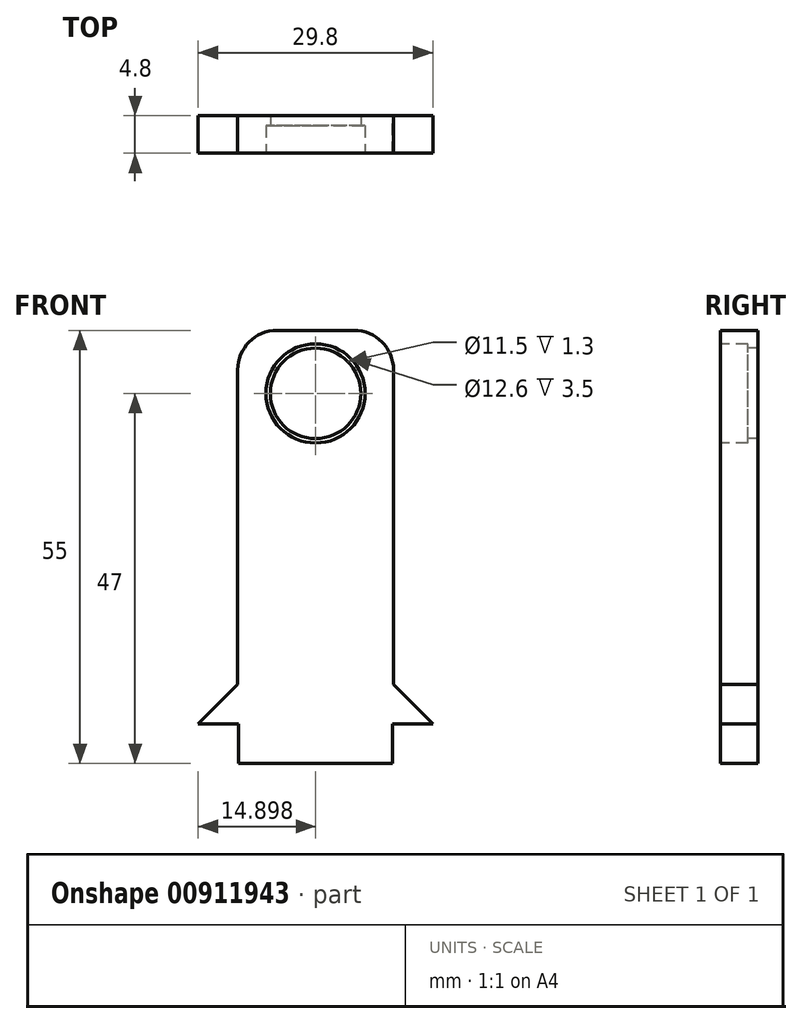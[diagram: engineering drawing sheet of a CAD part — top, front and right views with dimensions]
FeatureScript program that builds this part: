
annotation { "Feature Type Name" : "Feature", "Feature Type Description" : "" }
export const myFeature = defineFeature(function(context is Context, id is Id, definition is map)
    precondition{}
    {
        {
            var Q0;
            Q0=qCreatedBy(makeId("Front.planeOp"),FACE);
            var sketch = newSketch(context, id + "F0", { "sketchPlane" : qUnion([Q0])});
            skLineSegment(sketch, "E0.bottom", {"start": v(-10.83, 44.31) * mm, "end": v(8.97, 44.31) * mm});
            skLineSegment(sketch, "E0.top", {"start": v(-10.83, -10.69) * mm, "end": v(8.97, -10.69) * mm});
            skLineSegment(sketch, "E0.left", {"start": v(-10.83, 44.31) * mm, "end": v(-10.83, -10.69) * mm});
            skLineSegment(sketch, "E0.right", {"start": v(8.97, 44.31) * mm, "end": v(8.97, -10.69) * mm});
            skSolve(sketch);
        }
        {
            var Q0;
            Q0 = qSketchRegion(id + "F0", true);
            extrude(context, id + "F1", {"entities" : qUnion([Q0]), "depth" : 4.8 * mm, "offsetDistance" : 25 * mm});
        }
        {
            var Q0;
            Q0=makeQuery(id+"F1.opExtrude","CAP_FACE",FACE,{"disambiguationData":[OSD([sQuery(id+"F0.wireOp",EDGE,"E0.bottom"),sQuery(id+"F0.wireOp",EDGE,"E0.top"),sQuery(id+"F0.wireOp",EDGE,"E0.left"),sQuery(id+"F0.wireOp",EDGE,"E0.right")])],"isStart":false});
            var sketch = newSketch(context, id + "F2", { "sketchPlane" : qUnion([Q0])});
            skCircle(sketch, "E1", {"center": v(-0.93, 36.31) * mm, "radius": 5.75 * mm});
            skLineSegment(sketch, "E2", {"start": v(-0.93, -10.69) * mm, "end": v(-0.93, 44.31) * mm, "construction": true});
            skSolve(sketch);
        }
        {
            var Q0;
            Q0 = qSketchRegion(id + "F2", true);
            extrude(context, id + "F3", {"entities" : qUnion([Q0]), "operationType" : NewBodyOperationType.REMOVE, "endBound" : BoundingType.UP_TO_NEXT, "oppositeDirection" : true, "depth" : 25 * mm, "offsetDistance" : 25 * mm});
        }
        {
            var Q0;
            Q0=makeQuery(id+"F1.opExtrude","CAP_FACE",FACE,{"disambiguationData":[OSD([sQuery(id+"F0.wireOp",EDGE,"E0.bottom"),sQuery(id+"F0.wireOp",EDGE,"E0.top"),sQuery(id+"F0.wireOp",EDGE,"E0.left"),sQuery(id+"F0.wireOp",EDGE,"E0.right")])],"isStart":false});
            var sketch = newSketch(context, id + "F4", { "sketchPlane" : qUnion([Q0])});
            skCircle(sketch, "E3", {"center": v(-0.93, 36.31) * mm, "radius": 6.3 * mm});
            skSolve(sketch);
        }
        {
            var Q0;
            Q0 = qSketchRegion(id + "F4", true);
            extrude(context, id + "F5", {"entities" : qUnion([Q0]), "operationType" : NewBodyOperationType.REMOVE, "oppositeDirection" : true, "depth" : 3.5 * mm, "offsetDistance" : 25 * mm});
        }
        {
            var Q0;
            Q0=makeQuery(id+"F1.opExtrude","SWEPT_FACE",FACE,{"disambiguationData":[OSD([sQuery(id+"F0.wireOp",EDGE,"E0.left")])]});
            var sketch = newSketch(context, id + "F6", { "sketchPlane" : qUnion([Q0])});
            skLineSegment(sketch, "E4", {"start": v(2.4, -10.69) * mm, "end": v(2.4, -5.69) * mm, "construction": true});
            skLineSegment(sketch, "E5", {"start": v(4.8, -5.69) * mm, "end": v(0, -5.69) * mm});
            skLineSegment(sketch, "E6", {"start": v(0, -5.69) * mm, "end": v(0, -0.69) * mm});
            skLineSegment(sketch, "E7", {"start": v(0, -0.69) * mm, "end": v(4.8, -0.69) * mm});
            skLineSegment(sketch, "E8", {"start": v(4.8, -0.69) * mm, "end": v(4.8, -5.69) * mm});
            skSolve(sketch);
        }
        {
            var Q0;
            Q0 = qSketchRegion(id + "F6", true);
            extrude(context, id + "F7", {"entities" : qUnion([Q0]), "operationType" : NewBodyOperationType.ADD, "depth" : 5 * mm, "offsetDistance" : 25 * mm});
        }
        {
            var Q0;
            Q0=makeQuery(id+"F7.opExtrude","CAP_EDGE",EDGE,{"disambiguationData":[OSD([sQuery(id+"F6.wireOp",EDGE,"E7")])],"isStart":false});
            chamfer(context, id + "F8", {"entities" : qUnion([Q0]), "width" : 5 * mm, "tangentPropagation" : true});
        }
        {
            var Q0;
            Q0=makeQuery(id+"F1.opExtrude","SWEPT_FACE",FACE,{"disambiguationData":[OSD([sQuery(id+"F0.wireOp",EDGE,"E0.right")])]});
            var sketch = newSketch(context, id + "F9", { "sketchPlane" : qUnion([Q0])});
            skLineSegment(sketch, "E9", {"start": v(-2.4, -10.69) * mm, "end": v(-2.4, -5.69) * mm, "construction": true});
            skLineSegment(sketch, "E10", {"start": v(-4.8, -5.69) * mm, "end": v(0, -5.69) * mm});
            skLineSegment(sketch, "E11", {"start": v(-4.8, -5.69) * mm, "end": v(-4.8, -0.69) * mm});
            skLineSegment(sketch, "E12", {"start": v(-4.8, -0.69) * mm, "end": v(0, -0.69) * mm});
            skLineSegment(sketch, "E13", {"start": v(0, -0.69) * mm, "end": v(0, -5.69) * mm});
            skSolve(sketch);
        }
        {
            var Q0;
            Q0 = qSketchRegion(id + "F9", true);
            extrude(context, id + "F10", {"entities" : qUnion([Q0]), "operationType" : NewBodyOperationType.ADD, "depth" : 5 * mm, "offsetDistance" : 25 * mm});
        }
        {
            var Q0;
            Q0=makeQuery(id+"F10.opExtrude","CAP_EDGE",EDGE,{"disambiguationData":[OSD([sQuery(id+"F9.wireOp",EDGE,"E12")])],"isStart":false});
            chamfer(context, id + "F11", {"entities" : qUnion([Q0]), "width" : 5 * mm, "tangentPropagation" : true});
        }
        {
            var Q0;
            Q0=makeQuery(id+"F1.opExtrude","SWEPT_EDGE",EDGE,{"disambiguationData":[OSD([sQuery(id+"F0.wireOp",EDGE,"E0.bottom"),sQuery(id+"F0.wireOp",EDGE,"E0.left")])]});
            var Q1;
            Q1=makeQuery(id+"F1.opExtrude","SWEPT_EDGE",EDGE,{"disambiguationData":[OSD([sQuery(id+"F0.wireOp",EDGE,"E0.bottom"),sQuery(id+"F0.wireOp",EDGE,"E0.right")])]});
            fillet(context, id + "F12", {"entities" : qUnion([Q0, Q1]), "radius" : 5 * mm, "tangentPropagation" : true, "allowEdgeOverflow" : false});
        }
        {
            var Q0;
            {var subQ0=sQuery(id+"F0.wireOp",EDGE,"E0.top");var subQ2=sQuery(id+"F0.wireOp",EDGE,"E0.left");Q0=makeQuery(id+"F7.boolean.opBoolean","SPLIT",FACE,{"disambiguationData":[TD([makeQuery(id+"F1.opExtrude","SWEPT_FACE",FACE,{"disambiguationData":[OSD([subQ0])]})])],"derivedFrom":makeQuery(id+"F1.opExtrude","SWEPT_FACE",FACE,{"disambiguationData":[OSD([subQ2])]})});}
            extrude(context, id + "F13", {"entities" : qUnion([Q0]), "operationType" : NewBodyOperationType.REMOVE, "oppositeDirection" : true, "depth" : .1 * mm, "offsetDistance" : 25 * mm});
        }
        {
            var Q0;
            {var subQ0=sQuery(id+"F0.wireOp",EDGE,"E0.top");var subQ1=sQuery(id+"F0.wireOp",EDGE,"E0.right");Q0=makeQuery(id+"F10.boolean.opBoolean","SPLIT",FACE,{"disambiguationData":[TD([makeQuery(id+"F1.opExtrude","SWEPT_FACE",FACE,{"disambiguationData":[OSD([subQ0])]})])],"derivedFrom":makeQuery(id+"F1.opExtrude","SWEPT_FACE",FACE,{"disambiguationData":[OSD([subQ1])]})});}
            extrude(context, id + "F14", {"entities" : qUnion([Q0]), "operationType" : NewBodyOperationType.REMOVE, "oppositeDirection" : true, "depth" : 0.1 * mm, "offsetDistance" : 25 * mm});
        }
    });
